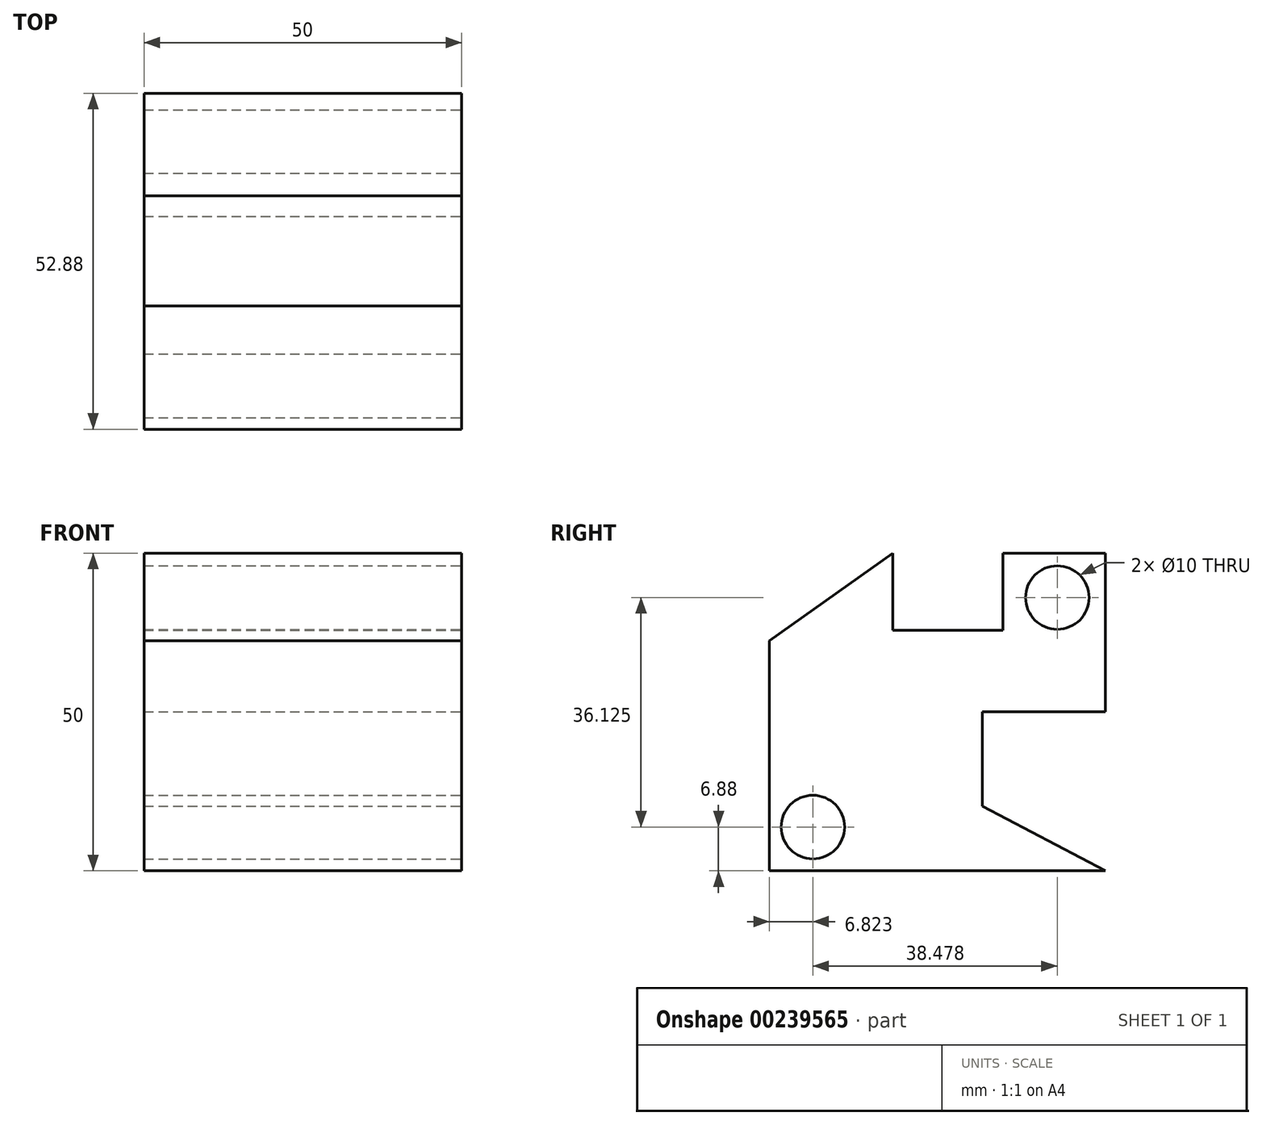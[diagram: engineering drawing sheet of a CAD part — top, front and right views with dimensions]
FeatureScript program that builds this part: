
annotation { "Feature Type Name" : "Feature", "Feature Type Description" : "" }
export const myFeature = defineFeature(function(context is Context, id is Id, definition is map)
    precondition{}
    {
        {
            var Q0;
            Q0=qCreatedBy(makeId("Top.planeOp"),FACE);
            var sketch = newSketch(context, id + "F0", { "sketchPlane" : qUnion([Q0])});
            skLineSegment(sketch, "E0.bottom", {"start": v(-19.85, 33.5) * mm, "end": v(30.15, 33.5) * mm});
            skLineSegment(sketch, "E0.top", {"start": v(-19.85, -19.38) * mm, "end": v(30.15, -19.38) * mm});
            skLineSegment(sketch, "E0.left", {"start": v(-19.85, 33.5) * mm, "end": v(-19.85, -19.38) * mm});
            skLineSegment(sketch, "E0.right", {"start": v(30.15, 33.5) * mm, "end": v(30.15, -19.38) * mm});
            skSolve(sketch);
        }
        {
            var Q0;
            Q0=makeQuery(id+"F0.imprint","IMPRINT",FACE,{"disambiguationData":[TD([[makeQuery(id+"F0.imprint","IMPRINT",EDGE,{"derivedFrom":sQuery(id+"F0.wireOp",EDGE,"E0.bottom")}),-1.0]])]});
            extrude(context, id + "F1", {"entities" : qUnion([Q0]), "depth" : 50 * mm});
        }
        {
            var Q0;
            Q0=makeQuery(id+"F1.opExtrude","SWEPT_FACE",FACE,{"disambiguationData":[OSD([sQuery(id+"F0.wireOp",EDGE,"E0.right")])]});
            var sketch = newSketch(context, id + "F2", { "sketchPlane" : qUnion([Q0])});
            skLineSegment(sketch, "E1", {"start": v(-19.38, 36.22) * mm, "end": v(0, 50) * mm});
            skSolve(sketch);
        }
        {
            var Q0;
            {var subQ0=sQuery(id+"F2.wireOp",EDGE,"E1");Q0=makeQuery(id+"F2.imprint","IMPRINT",FACE,{"disambiguationData":[TD([[makeQuery(id+"F2.imprint","IMPRINT",EDGE,{"derivedFrom":subQ0}),1.0]])]});}
            extrude(context, id + "F3", {"entities" : qUnion([Q0]), "operationType" : NewBodyOperationType.REMOVE, "oppositeDirection" : true, "depth" : 50 * mm});
        }
        {
            var Q0;
            Q0=makeQuery(id+"F1.opExtrude","SWEPT_FACE",FACE,{"disambiguationData":[OSD([sQuery(id+"F0.wireOp",EDGE,"E0.right")])]});
            var sketch = newSketch(context, id + "F4", { "sketchPlane" : qUnion([Q0])});
            skCircle(sketch, "E2", {"center": v(-12.56, 6.88) * mm, "radius": 5 * mm});
            skCircle(sketch, "E3", {"center": v(25.92, 43) * mm, "radius": 5 * mm});
            skSolve(sketch);
        }
        {
            var Q0;
            Q0 = qSketchRegion(id + "F4", true);
            extrude(context, id + "F5", {"entities" : qUnion([Q0]), "operationType" : NewBodyOperationType.REMOVE, "endBound" : BoundingType.THROUGH_ALL, "oppositeDirection" : true, "depth" : 51.05 * mm});
        }
        {
            var Q0;
            Q0=makeQuery(id+"F1.opExtrude","SWEPT_FACE",FACE,{"disambiguationData":[OSD([sQuery(id+"F0.wireOp",EDGE,"E0.right")])]});
            var sketch = newSketch(context, id + "F6", { "sketchPlane" : qUnion([Q0])});
            skLineSegment(sketch, "E4.bottom", {"start": v(0, 50) * mm, "end": v(17.35, 50) * mm});
            skLineSegment(sketch, "E4.top", {"start": v(0, 37.84) * mm, "end": v(17.35, 37.84) * mm});
            skLineSegment(sketch, "E4.left", {"start": v(0, 50) * mm, "end": v(0, 37.84) * mm});
            skLineSegment(sketch, "E4.right", {"start": v(17.35, 50) * mm, "end": v(17.35, 37.84) * mm});
            skLineSegment(sketch, "E5", {"start": v(33.5, 25) * mm, "end": v(14.13, 25) * mm});
            skLineSegment(sketch, "E6", {"start": v(14.13, 25) * mm, "end": v(14.13, 10.2) * mm});
            skLineSegment(sketch, "E7", {"start": v(14.13, 10.2) * mm, "end": v(33.5, 0) * mm});
            skLineSegment(sketch, "E8", {"start": v(33.5, 0) * mm, "end": v(33.5, 25) * mm});
            skSolve(sketch);
        }
        {
            var Q0;
            Q0=makeQuery(id+"F6.imprint","IMPRINT",FACE,{"disambiguationData":[TD([[makeQuery(id+"F6.imprint","IMPRINT",EDGE,{"derivedFrom":sQuery(id+"F6.wireOp",EDGE,"E5")}),1.0]])]});
            var Q1;
            Q1=makeQuery(id+"F6.imprint","IMPRINT",FACE,{"disambiguationData":[TD([[makeQuery(id+"F6.imprint","IMPRINT",EDGE,{"derivedFrom":sQuery(id+"F6.wireOp",EDGE,"E4.bottom")}),1.0]])]});
            extrude(context, id + "F7", {"entities" : qUnion([Q0, Q1]), "operationType" : NewBodyOperationType.REMOVE, "endBound" : BoundingType.THROUGH_ALL, "oppositeDirection" : true, "depth" : 25.4 * mm});
        }
    });
